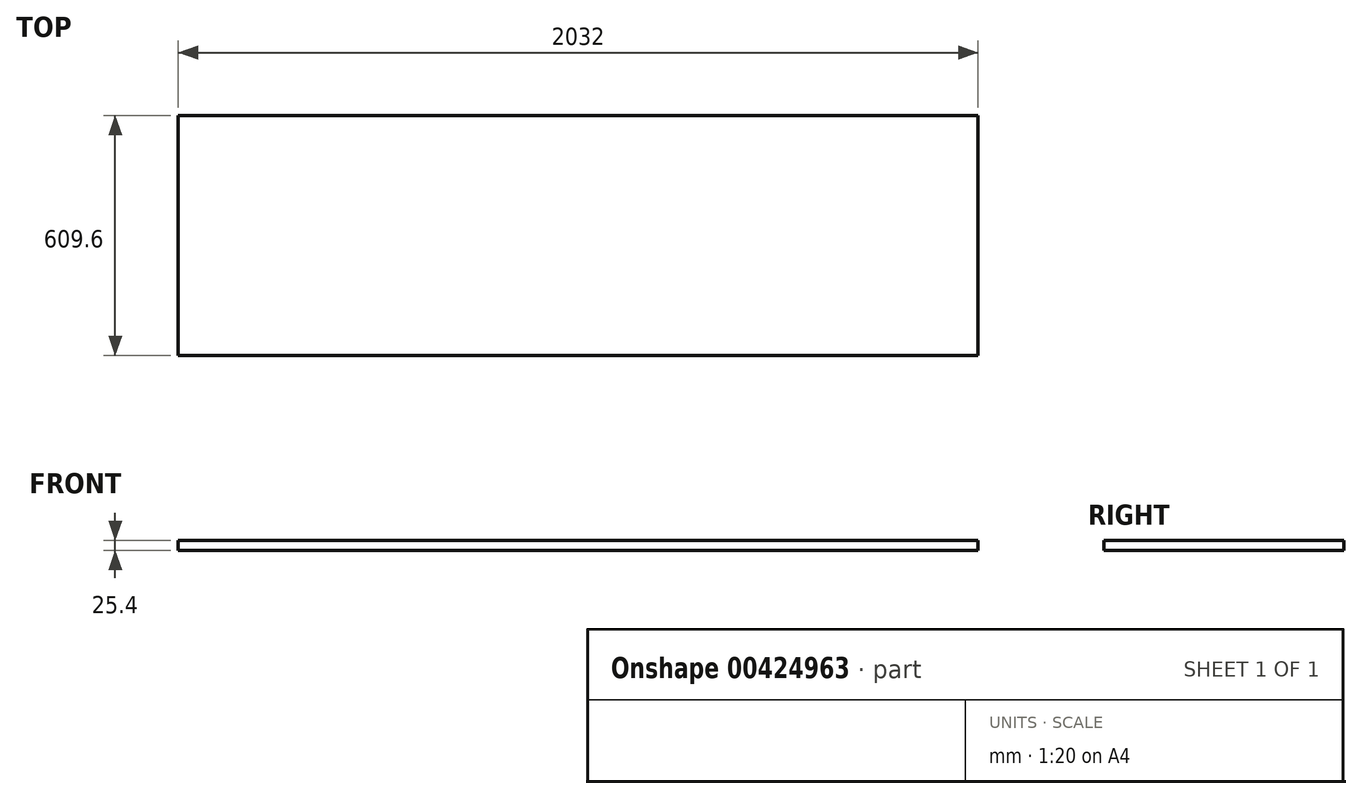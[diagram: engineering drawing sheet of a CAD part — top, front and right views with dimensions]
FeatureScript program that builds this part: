
annotation { "Feature Type Name" : "Feature", "Feature Type Description" : "" }
export const myFeature = defineFeature(function(context is Context, id is Id, definition is map)
    precondition{}
    {
        {
            var Q0;
            Q0=qCreatedBy(makeId("Top.planeOp"),FACE);
            var sketch = newSketch(context, id + "F0", { "sketchPlane" : qUnion([Q0])});
            skLineSegment(sketch, "E0.bottom", {"start": v(1016, 304.8) * mm, "end": v(-1016, 304.8) * mm});
            skLineSegment(sketch, "E0.top", {"start": v(1016, -304.8) * mm, "end": v(-1016, -304.8) * mm});
            skLineSegment(sketch, "E0.left", {"start": v(1016, 304.8) * mm, "end": v(1016, -304.8) * mm});
            skLineSegment(sketch, "E0.right", {"start": v(-1016, 304.8) * mm, "end": v(-1016, -304.8) * mm});
            skPoint(sketch, "E0.middle", {"position": v(0, 0) * mm});
            skSolve(sketch);
        }
        {
            var Q0;
            Q0 = qSketchRegion(id + "F0", true);
            extrude(context, id + "F1", {"entities" : qUnion([Q0]), "depth" : 25.4 * mm});
        }
    });
